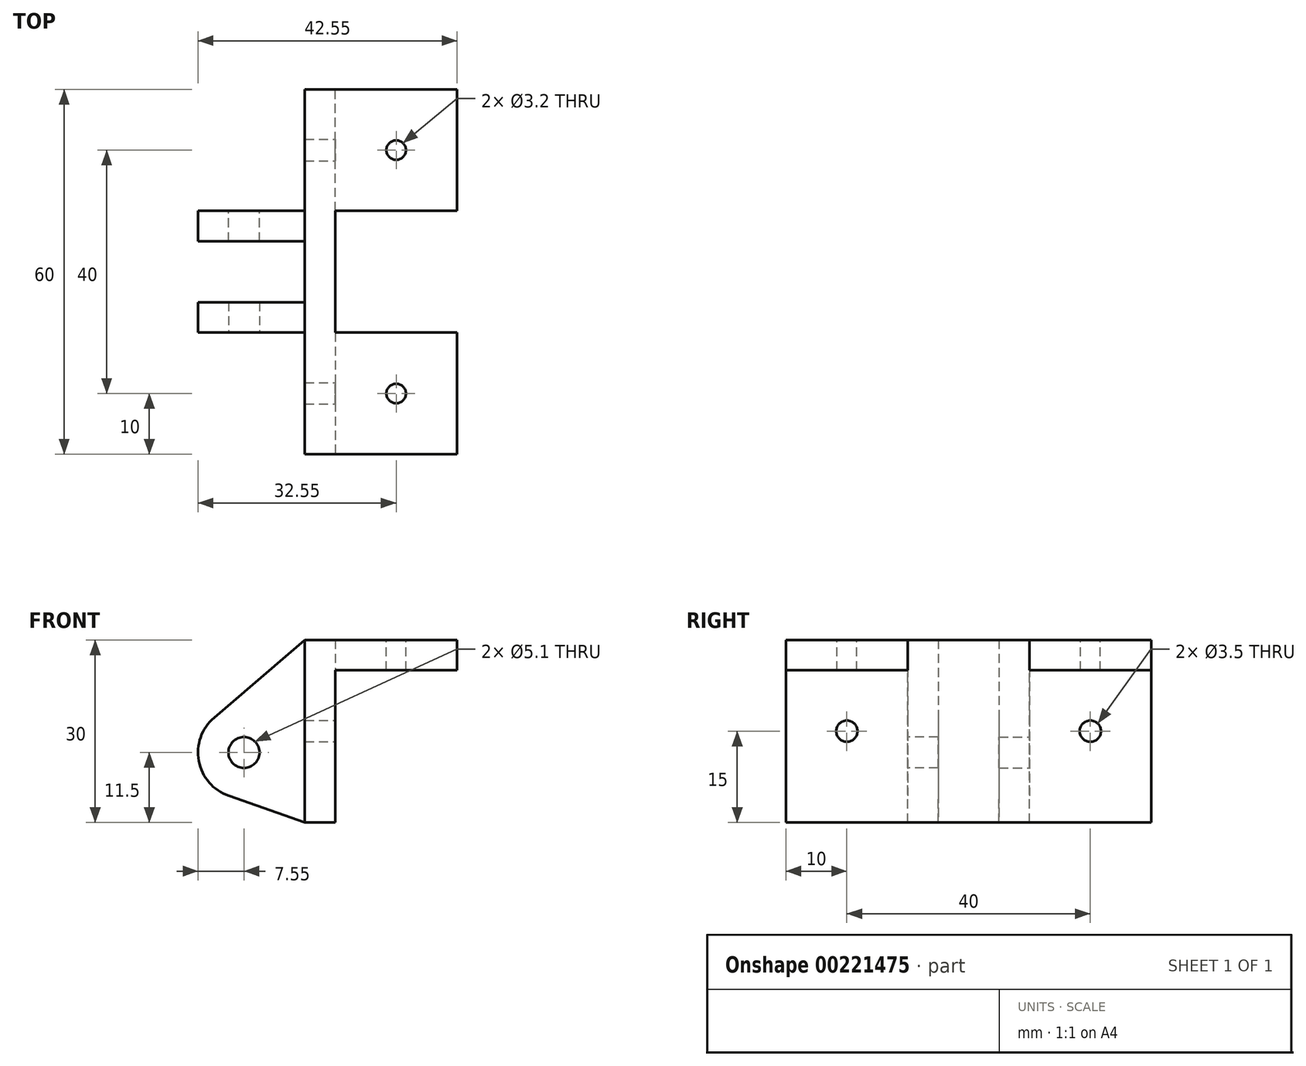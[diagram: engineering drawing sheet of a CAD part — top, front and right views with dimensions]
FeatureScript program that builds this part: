
annotation { "Feature Type Name" : "Feature", "Feature Type Description" : "" }
export const myFeature = defineFeature(function(context is Context, id is Id, definition is map)
    precondition{}
    {
        {
            var Q0;
            Q0=qCreatedBy(makeId("Front.planeOp"),FACE);
            var sketch = newSketch(context, id + "F0", { "sketchPlane" : qUnion([Q0])});
            skLineSegment(sketch, "E0", {"start": v(25, 0) * mm, "end": v(0, 0) * mm});
            skLineSegment(sketch, "E1", {"start": v(0, 0) * mm, "end": v(0, 30) * mm});
            skLineSegment(sketch, "E2", {"start": v(0, 30) * mm, "end": v(25, 30) * mm});
            skLineSegment(sketch, "E3", {"start": v(25, 30) * mm, "end": v(25, 25) * mm});
            skLineSegment(sketch, "E4", {"start": v(25, 25) * mm, "end": v(5, 25) * mm});
            skLineSegment(sketch, "E5", {"start": v(5, 25) * mm, "end": v(5, 5) * mm});
            skLineSegment(sketch, "E6", {"start": v(5, 5) * mm, "end": v(25, 5) * mm});
            skLineSegment(sketch, "E7", {"start": v(25, 5) * mm, "end": v(25, 0) * mm});
            skSolve(sketch);
        }
        {
            var Q0;
            Q0 = qSketchRegion(id + "F0", true);
            extrude(context, id + "F1", {"entities" : qUnion([Q0]), "depth" : 20 * mm});
        }
        {
            var Q0;
            Q0=makeQuery(id+"F1.opExtrude","SWEPT_FACE",FACE,{"disambiguationData":[OSD([sQuery(id+"F0.wireOp",EDGE,"E4")])]});
            var sketch = newSketch(context, id + "F2", { "sketchPlane" : qUnion([Q0])});
            skPoint(sketch, "E8", {"position": v(15, 10) * mm});
            skPoint(sketch, "E8.positionSnap0", {"position": v(25, 10) * mm});
            skPoint(sketch, "E8.positionSnap1", {"position": v(15, 20) * mm});
            skSolve(sketch);
        }
        {
            var Q0;
            Q0=makeQuery(id+"F1.opExtrude","SWEPT_FACE",FACE,{"disambiguationData":[OSD([sQuery(id+"F0.wireOp",EDGE,"E6")])]});
            var sketch = newSketch(context, id + "F3", { "sketchPlane" : qUnion([Q0])});
            skPoint(sketch, "E9", {"position": v(15, -10) * mm});
            skPoint(sketch, "E9.positionSnap0", {"position": v(25, -10) * mm});
            skPoint(sketch, "E9.positionSnap1", {"position": v(15, -20) * mm});
            skSolve(sketch);
        }
        {
            var Q0;
            Q0=sQuery(id+"F2.wireOp",VERTEX,"E8");
            var Q1;
            Q1=sQuery(id+"F3.wireOp",VERTEX,"E9");
            var Q2;
            Q2=makeQuery(id+"F1.opExtrude","SWEPT_BODY",BODY,{"disambiguationData":[OSD([sQuery(id+"F0.wireOp",EDGE,"E0"),sQuery(id+"F0.wireOp",EDGE,"E1"),sQuery(id+"F0.wireOp",EDGE,"E2"),sQuery(id+"F0.wireOp",EDGE,"E3"),sQuery(id+"F0.wireOp",EDGE,"E4"),sQuery(id+"F0.wireOp",EDGE,"E5"),sQuery(id+"F0.wireOp",EDGE,"E6"),sQuery(id+"F0.wireOp",EDGE,"E7")])]});
            hole(context, id + "F4", {"style" : HoleStyle.SIMPLE, "endStyle" : HoleEndStyle.THROUGH, "holeDiameter" : 3.2 * mm, "locations" : qUnion([Q0, Q1]), "scope" : qUnion([Q2]), "isTappedThrough" : true});
        }
        {
            var Q0;
            Q0=makeQuery(id+"F1.opExtrude","CAP_FACE",FACE,{"disambiguationData":[OSD([sQuery(id+"F0.wireOp",EDGE,"E0"),sQuery(id+"F0.wireOp",EDGE,"E1"),sQuery(id+"F0.wireOp",EDGE,"E2"),sQuery(id+"F0.wireOp",EDGE,"E3"),sQuery(id+"F0.wireOp",EDGE,"E4"),sQuery(id+"F0.wireOp",EDGE,"E5"),sQuery(id+"F0.wireOp",EDGE,"E6"),sQuery(id+"F0.wireOp",EDGE,"E7")])],"isStart":false});
            var sketch = newSketch(context, id + "F5", { "sketchPlane" : qUnion([Q0])});
            skCircle(sketch, "E10", {"center": v(-10, 11.5) * mm, "radius": 2.55 * mm});
            skLineSegment(sketch, "E11", {"start": v(0, 30) * mm, "end": v(-14.91, 17.24) * mm});
            skArc(sketch, "E12.0", {"start": v(-14.91, 17.24) * mm, "mid": v(-17.42, 10.1) * mm, "end": v(-12.5, 4.37) * mm});
            skLineSegment(sketch, "E13", {"start": v(0, 0) * mm, "end": v(-12.5, 4.37) * mm});
            skLineSegment(sketch, "E14", {"start": v(0, 0) * mm, "end": v(5, 0) * mm});
            skPoint(sketch, "E14.endSnap0", {"position": v(12.5, 0) * mm});
            skLineSegment(sketch, "E15", {"start": v(5, 0) * mm, "end": v(5, 30) * mm});
            skLineSegment(sketch, "E16", {"start": v(5, 30) * mm, "end": v(0, 30) * mm});
            skSolve(sketch);
        }
        {
            var Q0;
            {var subQ4=sQuery(id+"F5.wireOp",EDGE,"E14");Q0=makeQuery(id+"F5.imprint","IMPRINT",FACE,{"disambiguationData":[TD([[makeQuery(id+"F5.imprint","IMPRINT",EDGE,{"derivedFrom":subQ4}),-1.0]])]});}
            var Q1;
            Q1=makeQuery(id+"F5.imprint","IMPRINT",FACE,{"disambiguationData":[TD([[makeQuery(id+"F5.imprint","IMPRINT",EDGE,{"derivedFrom":sQuery(id+"F5.wireOp",EDGE,"E10")}),-1.0]])]});
            extrude(context, id + "F6", {"entities" : qUnion([Q0, Q1]), "operationType" : NewBodyOperationType.ADD, "depth" : 5 * mm});
        }
        {
            var Q0;
            Q0=makeQuery(id+"F6.opExtrude","CAP_FACE",FACE,{"disambiguationData":[OSD([sQuery(id+"F5.wireOp",EDGE,"E10"),sQuery(id+"F5.wireOp",EDGE,"E11"),sQuery(id+"F5.wireOp",EDGE,"E12.0"),sQuery(id+"F5.wireOp",EDGE,"E13"),sQuery(id+"F5.wireOp",EDGE,"E14"),sQuery(id+"F5.wireOp",EDGE,"E15"),sQuery(id+"F5.wireOp",EDGE,"E16")])],"isStart":false});
            var sketch = newSketch(context, id + "F7", { "sketchPlane" : qUnion([Q0])});
            skLineSegment(sketch, "E17.bottom", {"start": v(0, 30) * mm, "end": v(5, 30) * mm});
            skLineSegment(sketch, "E17.top", {"start": v(0, 0) * mm, "end": v(5, 0) * mm});
            skLineSegment(sketch, "E17.left", {"start": v(0, 30) * mm, "end": v(0, 0) * mm});
            skLineSegment(sketch, "E17.right", {"start": v(5, 30) * mm, "end": v(5, 0) * mm});
            skSolve(sketch);
        }
        {
            var Q0;
            Q0=makeQuery(id+"F7.imprint","IMPRINT",FACE,{"disambiguationData":[TD([[makeQuery(id+"F7.imprint","IMPRINT",EDGE,{"derivedFrom":sQuery(id+"F7.wireOp",EDGE,"E17.bottom")}),-1.0]])]});
            extrude(context, id + "F8", {"entities" : qUnion([Q0]), "operationType" : NewBodyOperationType.ADD, "depth" : 5 * mm});
        }
        {
            var Q0;
            Q0=makeQuery(id+"F1.opExtrude","SWEPT_BODY",BODY,{"disambiguationData":[OSD([sQuery(id+"F0.wireOp",EDGE,"E0"),sQuery(id+"F0.wireOp",EDGE,"E1"),sQuery(id+"F0.wireOp",EDGE,"E2"),sQuery(id+"F0.wireOp",EDGE,"E3"),sQuery(id+"F0.wireOp",EDGE,"E4"),sQuery(id+"F0.wireOp",EDGE,"E5"),sQuery(id+"F0.wireOp",EDGE,"E6"),sQuery(id+"F0.wireOp",EDGE,"E7")])]});
            var Q1;
            Q1=makeQuery(id+"F8.opExtrude","CAP_FACE",FACE,{"disambiguationData":[OSD([sQuery(id+"F7.wireOp",EDGE,"E17.bottom"),sQuery(id+"F7.wireOp",EDGE,"E17.top"),sQuery(id+"F7.wireOp",EDGE,"E17.left"),sQuery(id+"F7.wireOp",EDGE,"E17.right")])],"isStart":false});
            mirror(context, id + "F9", {"operationType" : NewBodyOperationType.ADD, "entities" : qUnion([Q0]), "mirrorPlane" : qUnion([Q1])});
        }
        {
            var Q0;
            Q0=makeQuery(id+"F9.opPattern","COPY",FACE,{"derivedFrom":makeQuery(id+"F1.opExtrude","SWEPT_FACE",FACE,{"disambiguationData":[OSD([sQuery(id+"F0.wireOp",EDGE,"E6")])]}),"instanceName":"1"});
            var sketch = newSketch(context, id + "F10", { "sketchPlane" : qUnion([Q0])});
            skLineSegment(sketch, "E18.bottom", {"start": v(25, -60) * mm, "end": v(5, -60) * mm});
            skLineSegment(sketch, "E18.top", {"start": v(25, 0) * mm, "end": v(5, 0) * mm});
            skLineSegment(sketch, "E18.left", {"start": v(25, -60) * mm, "end": v(25, 0) * mm});
            skLineSegment(sketch, "E18.right", {"start": v(5, -60) * mm, "end": v(5, 0) * mm});
            skSolve(sketch);
        }
        {
            var Q0;
            {var subQ0=sQuery(id+"F10.wireOp",EDGE,"E18.top");Q0=makeQuery(id+"F10.imprint","IMPRINT",FACE,{"disambiguationData":[TD([[makeQuery(id+"F10.imprint","IMPRINT",EDGE,{"derivedFrom":subQ0}),1.0]])]});}
            var Q1;
            {var subQ2=sQuery(id+"F10.wireOp",EDGE,"E18.bottom");Q1=makeQuery(id+"F10.imprint","IMPRINT",FACE,{"disambiguationData":[TD([[makeQuery(id+"F10.imprint","IMPRINT",EDGE,{"derivedFrom":subQ2}),1.0]])]});}
            var Q2;
            {var subQ0=makeQuery(id+"F8.boolean.opBoolean","MERGE",FACE,{"derivedFrom":[makeQuery(id+"F6.boolean.opBoolean","MERGE",FACE,{"derivedFrom":[makeQuery(id+"F1.opExtrude","SWEPT_FACE",FACE,{"disambiguationData":[OSD([sQuery(id+"F0.wireOp",EDGE,"E0")])]}),makeQuery(id+"F6.opExtrude","SWEPT_FACE",FACE,{"disambiguationData":[OSD([sQuery(id+"F5.wireOp",EDGE,"E14")])]})]}),makeQuery(id+"F8.opExtrude","SWEPT_FACE",FACE,{"disambiguationData":[OSD([sQuery(id+"F7.wireOp",EDGE,"E17.top")])]})]});Q2=makeQuery(id+"F9.boolean.opBoolean","MERGE",FACE,{"derivedFrom":[subQ0,makeQuery(id+"F9.opPattern","COPY",FACE,{"derivedFrom":subQ0,"instanceName":"1"})]});}
            extrude(context, id + "F11", {"entities" : qUnion([Q0, Q1]), "operationType" : NewBodyOperationType.REMOVE, "endBound" : BoundingType.UP_TO_SURFACE, "oppositeDirection" : true, "endBoundEntityFace" : qUnion([Q2]), "depth" : 25 * mm});
        }
        {
            var Q0;
            Q0=makeQuery(id+"F1.opExtrude","SWEPT_FACE",FACE,{"disambiguationData":[OSD([sQuery(id+"F0.wireOp",EDGE,"E1")])]});
            var sketch = newSketch(context, id + "F12", { "sketchPlane" : qUnion([Q0])});
            skPoint(sketch, "E19", {"position": v(10, 15) * mm});
            skPoint(sketch, "E20", {"position": v(50, 15) * mm});
            skSolve(sketch);
        }
        {
            var Q0;
            Q0=sQuery(id+"F12.wireOp",VERTEX,"E19");
            var Q1;
            Q1=sQuery(id+"F12.wireOp",VERTEX,"E20");
            var Q2;
            Q2=makeQuery(id+"F1.opExtrude","SWEPT_BODY",BODY,{"disambiguationData":[OSD([sQuery(id+"F0.wireOp",EDGE,"E0"),sQuery(id+"F0.wireOp",EDGE,"E1"),sQuery(id+"F0.wireOp",EDGE,"E2"),sQuery(id+"F0.wireOp",EDGE,"E3"),sQuery(id+"F0.wireOp",EDGE,"E4"),sQuery(id+"F0.wireOp",EDGE,"E5"),sQuery(id+"F0.wireOp",EDGE,"E6"),sQuery(id+"F0.wireOp",EDGE,"E7")])]});
            hole(context, id + "F13", {"style" : HoleStyle.SIMPLE, "endStyle" : HoleEndStyle.BLIND, "holeDiameter" : 3.5 * mm, "holeDepth" : 10 * mm, "tappedDepth" : 12 * mm, "tapClearance" : 3, "locations" : qUnion([Q0, Q1]), "scope" : qUnion([Q2])});
        }
    });
